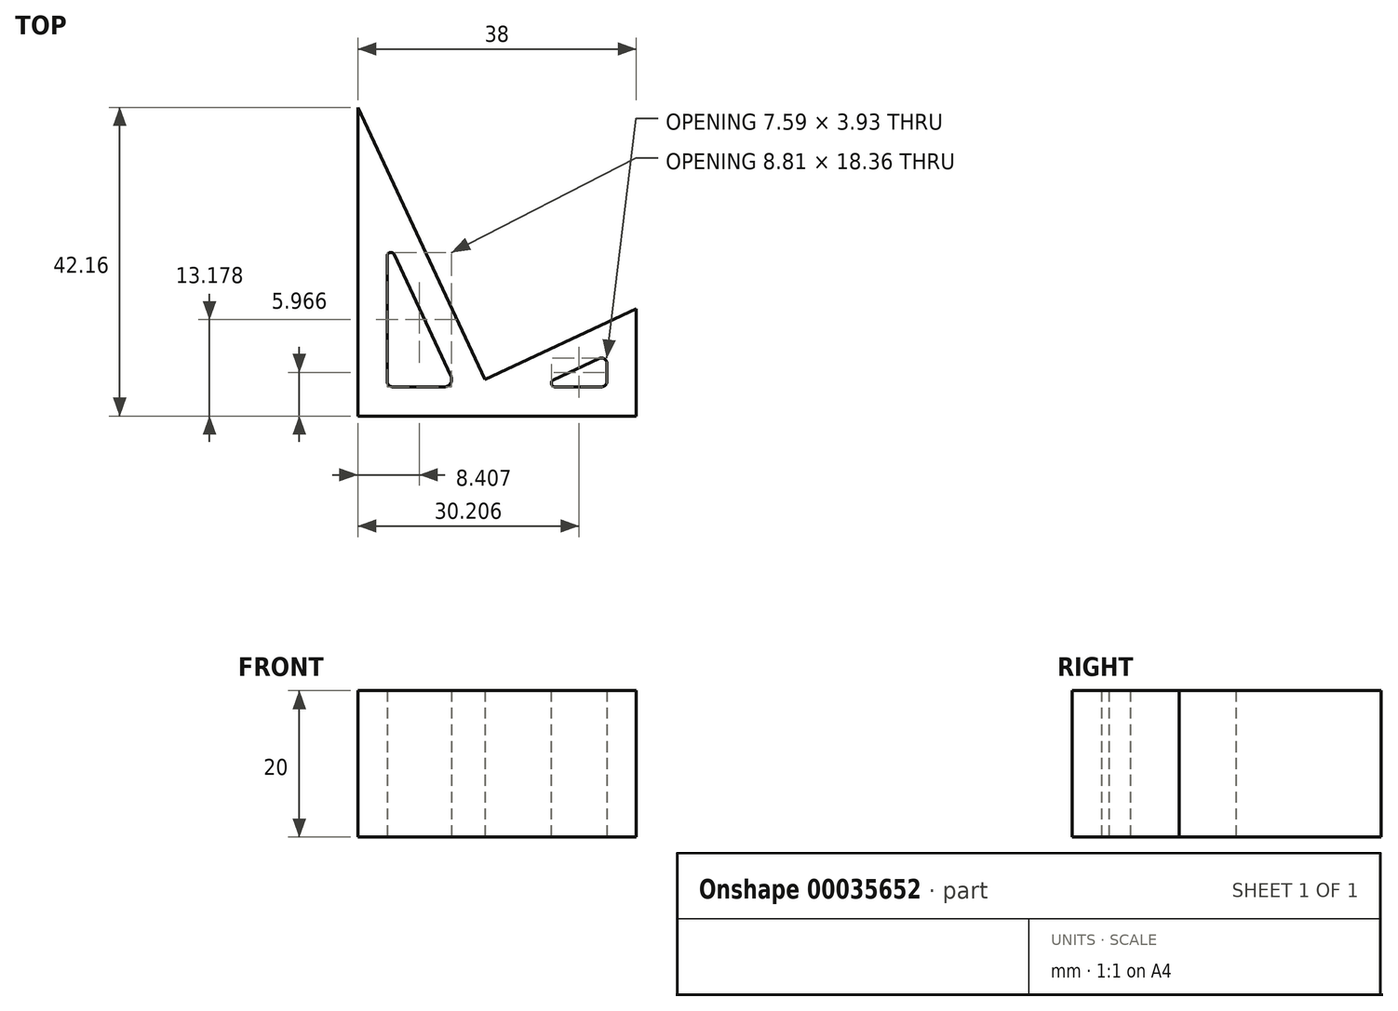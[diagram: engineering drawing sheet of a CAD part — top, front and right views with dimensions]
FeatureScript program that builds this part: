
annotation { "Feature Type Name" : "Feature", "Feature Type Description" : "" }
export const myFeature = defineFeature(function(context is Context, id is Id, definition is map)
    precondition{}
    {
        {
            var Q0;
            Q0=qCreatedBy(makeId("Top.planeOp"),FACE);
            var sketch = newSketch(context, id + "F0", { "sketchPlane" : qUnion([Q0])});
            skLineSegment(sketch, "E0", {"start": v(0, 0) * mm, "end": v(-17.33, 0) * mm});
            skLineSegment(sketch, "E1", {"start": v(-17.33, 0) * mm, "end": v(-17.33, 42.16) * mm});
            skLineSegment(sketch, "E2", {"start": v(-17.33, 42.16) * mm, "end": v(0, 5) * mm});
            skLineSegment(sketch, "E3", {"start": v(0, 5) * mm, "end": v(20.67, 14.64) * mm});
            skLineSegment(sketch, "E4", {"start": v(20.67, 14.64) * mm, "end": v(20.67, 0) * mm});
            skLineSegment(sketch, "E5", {"start": v(20.67, 0) * mm, "end": v(0, 0) * mm});
            skSolve(sketch);
        }
        {
            var Q0;
            Q0=makeQuery(id+"F0.imprint","IMPRINT",FACE,{"disambiguationData":[TD([[makeQuery(id+"F0.imprint","IMPRINT",EDGE,{"derivedFrom":sQuery(id+"F0.wireOp",EDGE,"E0")}),-1.0]])]});
            extrude(context, id + "F1", {"entities" : qUnion([Q0]), "depth" : 20 * mm});
        }
        {
            var Q0;
            Q0=qCreatedBy(makeId("Top.planeOp"),FACE);
            var sketch = newSketch(context, id + "F2", { "sketchPlane" : qUnion([Q0])});
            skLineSegment(sketch, "E6.0.0", {"start": v(-17.33, 0) * mm, "end": v(20.67, 0) * mm});
            skLineSegment(sketch, "E6.0.1", {"start": v(20.67, 0) * mm, "end": v(20.67, 14.64) * mm});
            skLineSegment(sketch, "E6.0.2", {"start": v(20.67, 14.64) * mm, "end": v(0, 5) * mm});
            skLineSegment(sketch, "E6.0.3", {"start": v(0, 5) * mm, "end": v(-17.33, 42.16) * mm});
            skLineSegment(sketch, "E6.0.4", {"start": v(-17.33, 42.16) * mm, "end": v(-17.33, 0) * mm});
            skLineSegment(sketch, "E7.0", {"start": v(15.6, 7.86) * mm, "end": v(9.36, 4.95) * mm});
            skLineSegment(sketch, "E7.1", {"start": v(9.58, 4) * mm, "end": v(15.92, 4) * mm});
            skLineSegment(sketch, "E7.2", {"start": v(-12.58, 4) * mm, "end": v(-5.52, 4) * mm});
            skLineSegment(sketch, "E7.3", {"start": v(-13.33, 21.86) * mm, "end": v(-13.33, 4.75) * mm});
            skLineSegment(sketch, "E7.4", {"start": v(16.67, 4.75) * mm, "end": v(16.67, 7.18) * mm});
            skLineSegment(sketch, "E7.5", {"start": v(-4.61, 5.42) * mm, "end": v(-12.37, 22.07) * mm});
            skPoint(sketch, "E8.visualSharp", {"position": v(-13.33, 24.12) * mm});
            skArc(sketch, "E8.filletArc", {"start": v(-12.37, 22.07) * mm, "mid": v(-12.94, 22.35) * mm, "end": v(-13.33, 21.86) * mm});
            skPoint(sketch, "E9.visualSharp", {"position": v(-13.33, 4) * mm});
            skArc(sketch, "E9.filletArc", {"start": v(-13.33, 4.75) * mm, "mid": v(-13.1, 4.22) * mm, "end": v(-12.58, 4) * mm});
            skPoint(sketch, "E10.visualSharp", {"position": v(-3.95, 4) * mm});
            skArc(sketch, "E10.filletArc", {"start": v(-5.52, 4) * mm, "mid": v(-4.67, 4.46) * mm, "end": v(-4.61, 5.42) * mm});
            skPoint(sketch, "E11.visualSharp", {"position": v(7.32, 4) * mm});
            skArc(sketch, "E11.filletArc", {"start": v(9.36, 4.95) * mm, "mid": v(9.09, 4.4) * mm, "end": v(9.58, 4) * mm});
            skPoint(sketch, "E12.visualSharp", {"position": v(16.67, 4) * mm});
            skArc(sketch, "E12.filletArc", {"start": v(15.92, 4) * mm, "mid": v(16.45, 4.22) * mm, "end": v(16.67, 4.75) * mm});
            skPoint(sketch, "E13.visualSharp", {"position": v(16.67, 8.36) * mm});
            skArc(sketch, "E13.filletArc", {"start": v(16.67, 7.18) * mm, "mid": v(16.33, 7.82) * mm, "end": v(15.6, 7.86) * mm});
            skSolve(sketch);
        }
        {
            var Q0;
            Q0=makeQuery(id+"F2.imprint","IMPRINT",FACE,{"disambiguationData":[TD([[makeQuery(id+"F2.imprint","IMPRINT",EDGE,{"derivedFrom":sQuery(id+"F2.wireOp",EDGE,"E7.2")}),1.0]])]});
            var Q1;
            Q1=makeQuery(id+"F2.imprint","IMPRINT",FACE,{"disambiguationData":[TD([[makeQuery(id+"F2.imprint","IMPRINT",EDGE,{"derivedFrom":sQuery(id+"F2.wireOp",EDGE,"E7.0")}),1.0]])]});
            extrude(context, id + "F3", {"entities" : qUnion([Q0, Q1]), "operationType" : NewBodyOperationType.REMOVE, "depth" : 25 * mm});
        }
    });
